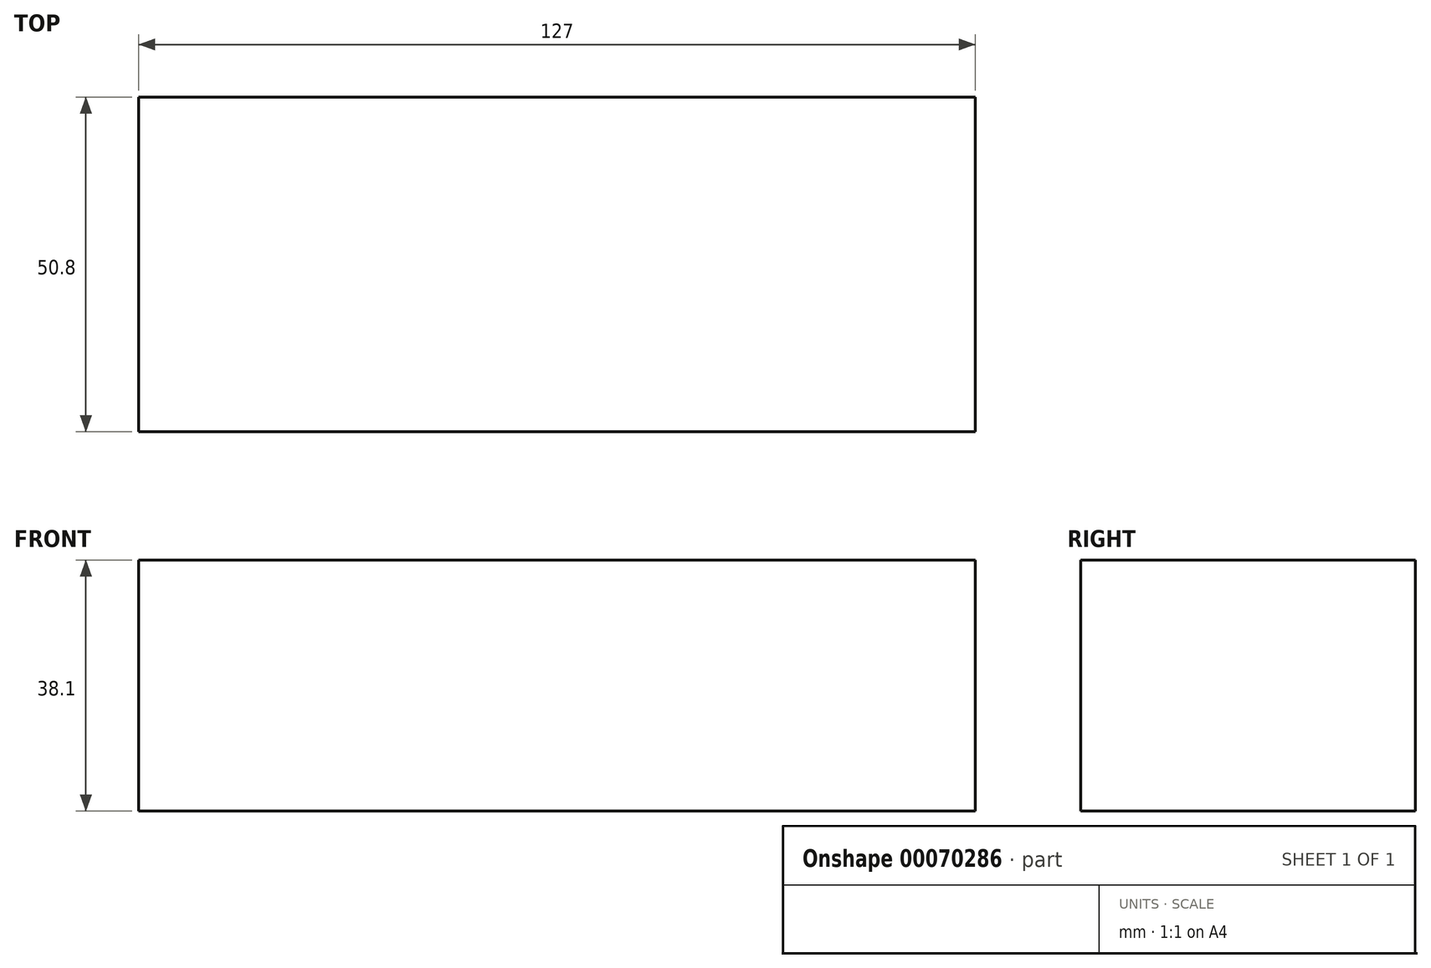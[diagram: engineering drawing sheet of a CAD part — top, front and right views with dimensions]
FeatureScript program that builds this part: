
annotation { "Feature Type Name" : "Feature", "Feature Type Description" : "" }
export const myFeature = defineFeature(function(context is Context, id is Id, definition is map)
    precondition{}
    {
        {
            var Q0;
            Q0=qCreatedBy(makeId("Top.planeOp"),FACE);
            var sketch = newSketch(context, id + "F0", { "sketchPlane" : qUnion([Q0])});
            skLineSegment(sketch, "E0.bottom", {"start": v(0, 0) * mm, "end": v(127, 0) * mm});
            skLineSegment(sketch, "E0.top", {"start": v(0, 50.8) * mm, "end": v(127, 50.8) * mm});
            skLineSegment(sketch, "E0.left", {"start": v(0, 0) * mm, "end": v(0, 50.8) * mm});
            skLineSegment(sketch, "E0.right", {"start": v(127, 0) * mm, "end": v(127, 50.8) * mm});
            skSolve(sketch);
        }
        {
            var Q0;
            Q0 = qSketchRegion(id + "F0", true);
            extrude(context, id + "F1", {"entities" : qUnion([Q0]), "depth" : 38.1 * mm});
        }
    });
